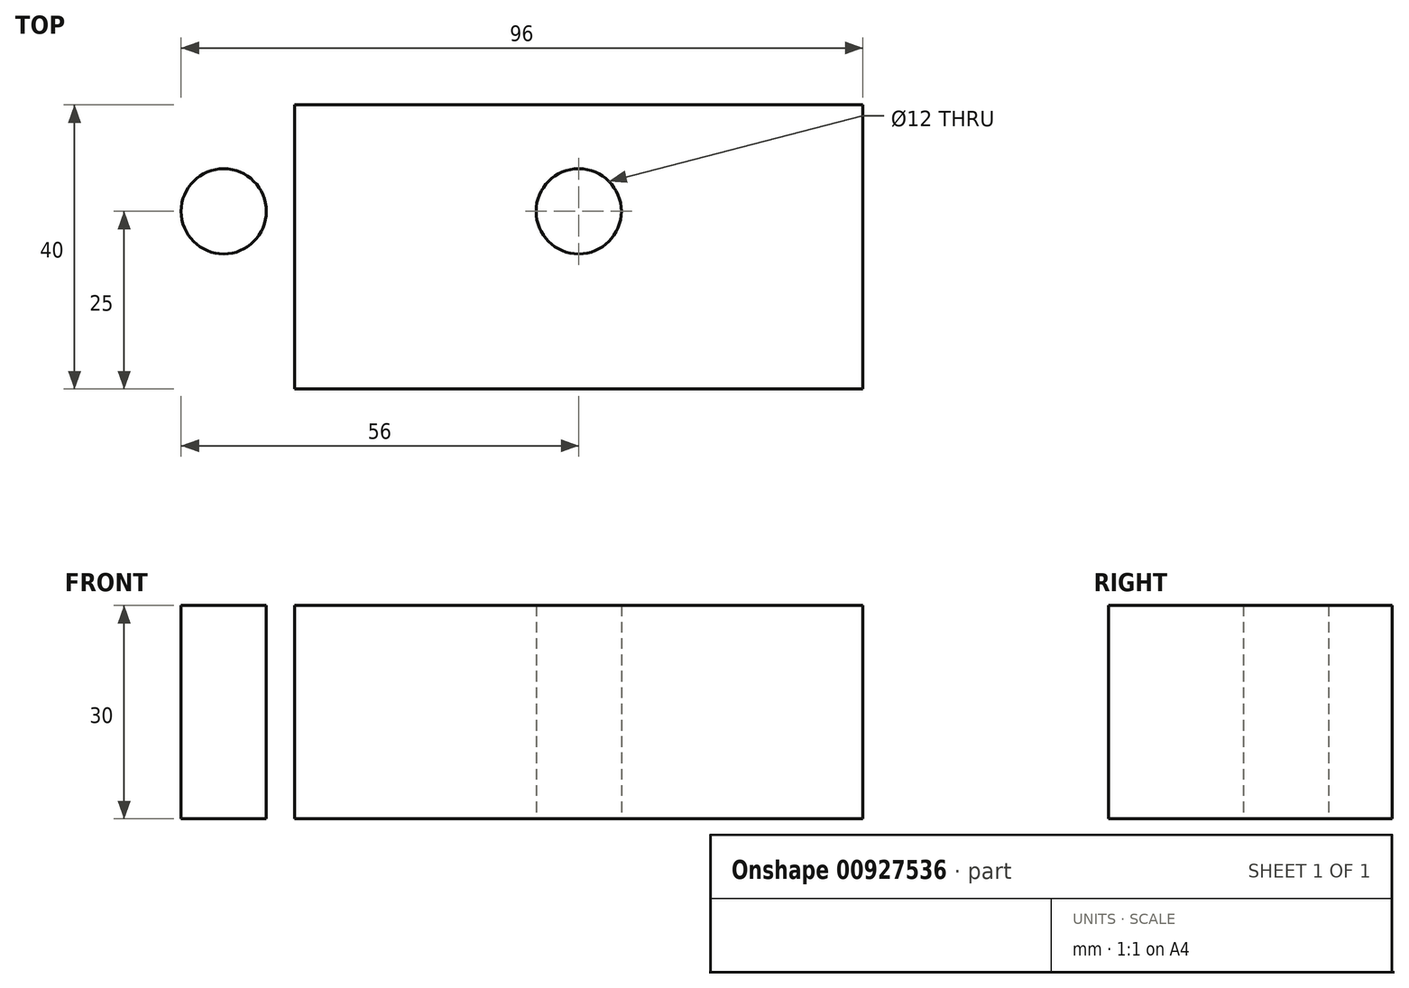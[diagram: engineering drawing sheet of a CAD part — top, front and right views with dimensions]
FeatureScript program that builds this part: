
annotation { "Feature Type Name" : "Feature", "Feature Type Description" : "" }
export const myFeature = defineFeature(function(context is Context, id is Id, definition is map)
    precondition{}
    {
        {
            var Q0;
            Q0=qCreatedBy(makeId("Front.planeOp"),FACE);
            var sketch = newSketch(context, id + "F0", { "sketchPlane" : qUnion([Q0])});
            skLineSegment(sketch, "E0.bottom", {"start": v(-120, 30) * mm, "end": v(0, 30) * mm});
            skLineSegment(sketch, "E0.top", {"start": v(-120, 0) * mm, "end": v(0, 0) * mm});
            skLineSegment(sketch, "E0.left", {"start": v(-120, 30) * mm, "end": v(-120, 0) * mm});
            skLineSegment(sketch, "E0.right", {"start": v(0, 30) * mm, "end": v(0, 0) * mm});
            skSolve(sketch);
        }
        {
            var Q0;
            Q0 = qSketchRegion(id + "F0", true);
            extrude(context, id + "F1", {"entities" : qUnion([Q0]), "depth" : 50 * mm, "offsetDistance" : 25 * mm});
        }
        {
            var Q0;
            Q0=makeQuery(id+"F1.opExtrude","SWEPT_FACE",FACE,{"disambiguationData":[OSD([sQuery(id+"F0.wireOp",EDGE,"E0.top")])]});
            var sketch = newSketch(context, id + "F2", { "sketchPlane" : qUnion([Q0])});
            skLineSegment(sketch, "E1", {"start": v(-137.39, 25) * mm, "end": v(26.27, 25) * mm, "construction": true});
            skLineSegment(sketch, "E2", {"start": v(-60, 89.72) * mm, "end": v(-60, -29.8) * mm, "construction": true});
            skCircle(sketch, "E3", {"center": v(-10, 25) * mm, "radius": 6 * mm});
            skCircle(sketch, "E4.MirrorC", {"center": v(-110, 25) * mm, "radius": 6 * mm});
            skLineSegment(sketch, "E5.bottom", {"start": v(-100, 50) * mm, "end": v(-20, 50) * mm});
            skLineSegment(sketch, "E5.top", {"start": v(-100, 10) * mm, "end": v(-20, 10) * mm});
            skLineSegment(sketch, "E5.left", {"start": v(-100, 50) * mm, "end": v(-100, 10) * mm});
            skLineSegment(sketch, "E5.right", {"start": v(-20, 50) * mm, "end": v(-20, 10) * mm});
            skCircle(sketch, "E6", {"center": v(-60, 25) * mm, "radius": 6 * mm});
            skSolve(sketch);
        }
        {
            var Q0;
            Q0=makeQuery(id+"F2.imprint","IMPRINT",FACE,{"disambiguationData":[TD([[makeQuery(id+"F2.imprint","IMPRINT",EDGE,{"derivedFrom":sQuery(id+"F2.wireOp",EDGE,"E4.MirrorC")}),-1.0]])]});
            var Q1;
            Q1=makeQuery(id+"F2.imprint","IMPRINT",FACE,{"disambiguationData":[TD([[makeQuery(id+"F2.imprint","IMPRINT",EDGE,{"derivedFrom":sQuery(id+"F2.wireOp",EDGE,"E3")}),1.0]])]});
            var Q2;
            Q2=makeQuery(id+"F2.imprint","IMPRINT",FACE,{"disambiguationData":[TD([[makeQuery(id+"F2.imprint","IMPRINT",EDGE,{"derivedFrom":sQuery(id+"F2.wireOp",EDGE,"E6")}),1.0]])]});
            extrude(context, id + "F3", {"entities" : qUnion([Q0, Q1, Q2]), "operationType" : NewBodyOperationType.REMOVE, "endBound" : BoundingType.THROUGH_ALL, "oppositeDirection" : true, "depth" : 25 * mm, "offsetDistance" : 25 * mm});
        }
    });
